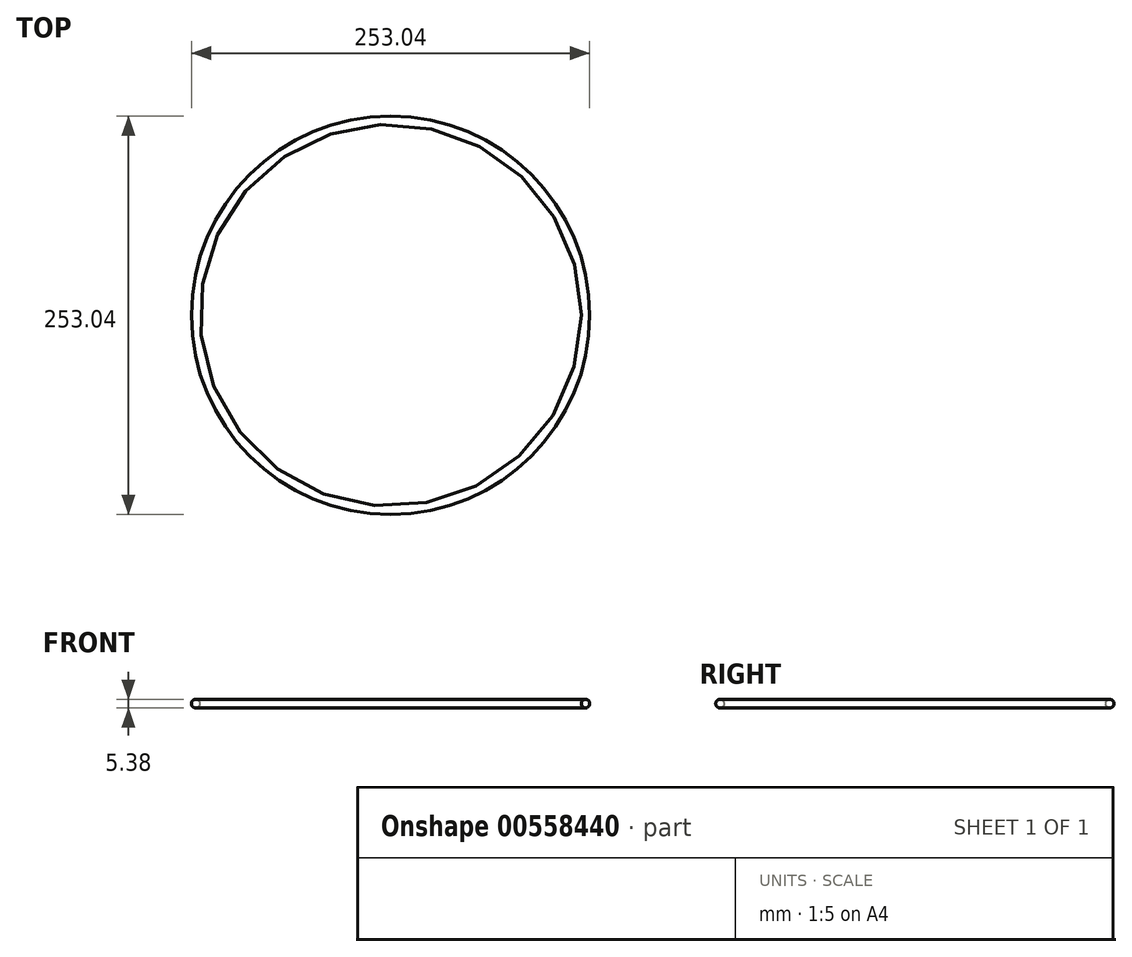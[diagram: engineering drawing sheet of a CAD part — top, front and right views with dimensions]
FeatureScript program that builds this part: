
annotation { "Feature Type Name" : "Feature", "Feature Type Description" : "" }
export const myFeature = defineFeature(function(context is Context, id is Id, definition is map)
    precondition{}
    {
        {
            var Q0;
            Q0=qCreatedBy(makeId("Top.planeOp"),FACE);
            var sketch = newSketch(context, id + "F0", { "sketchPlane" : qUnion([Q0])});
            skCircle(sketch, "E0", {"center": v(0, 0) * mm, "radius": 123.83 * mm});
            skSolve(sketch);
        }
        {
            var Q0;
            Q0=qCreatedBy(makeId("Front.planeOp"),FACE);
            var sketch = newSketch(context, id + "F1", { "sketchPlane" : qUnion([Q0])});
            skCircle(sketch, "E1", {"center": v(-123.83, 0) * mm, "radius": 2.7 * mm});
            skSolve(sketch);
        }
        {
            var Q0;
            Q0=makeQuery(id+"F1.imprint","IMPRINT",FACE,{"disambiguationData":[TD([[makeQuery(id+"F1.imprint","IMPRINT",EDGE,{"derivedFrom":sQuery(id+"F1.wireOp",EDGE,"E1")}),1.0]])]});
            var Q1;
            Q1=sQuery(id+"F0.wireOp",EDGE,"E0");
            sweep(context, id + "F2", {"profiles" : qUnion([Q0]), "path" : qUnion([Q1])});
        }
    });
